# Revit family: Lighting_Device-Digital_Timer-Hubbell_Wiring-DT2000W
name_source: partatom
category: Lighting Devices
revit_build: Autodesk Revit 2015 (Build: 20140606_1530(x64)
units: mm (PartAtom-declared; Revit-internal decimal feet)

## types (2) — shared parameters
Certifications = UL, cULus,  CEC Title 24
Connector Description 1 = Power Supply
Connector Description 2 = Controls
Default Elevation = 48 "
Description = H-MOSS® Controls Digital Timer Wall Switch
Frequency = 60 Hz
Height = 1.68 "
Humidity = 20% to 90% non condensing relative humidity
Length = 1.28 "
Load Classification = Lighting
Manufacturer = Hubbell Wiring Device-Kellems
Model = DT2000W
Number of Poles = 1
Operating Temperature = 32°F to 104°F (0°C to 40°C)
Power Factor = 1
Product Documentation Link = http://ecatalog.hubbell-wiring.com
Product Material = Plastic - Hubbell - White
Product Page URL = http://ecatalog.hubbell-wiring.com
Product data url = https://bimobject.com
Time Delays = Adjustable to up to 4 hours
UPC Number = 783585413020
URL = http://www.hubbell-wiring.com
Width = 2.68 "

## per-type parameters (varying)
| type | Apparent Load | Voltage | Wattage |
| 120V | 960.000 VA | 120 V | 960 W |
| 277V | 1200.000 VA | 277 V | 1200 W |

## geometry (parser evidence)
native form markers: Blend x4, Sweep x2
no freeform markers — native parametric forms only
